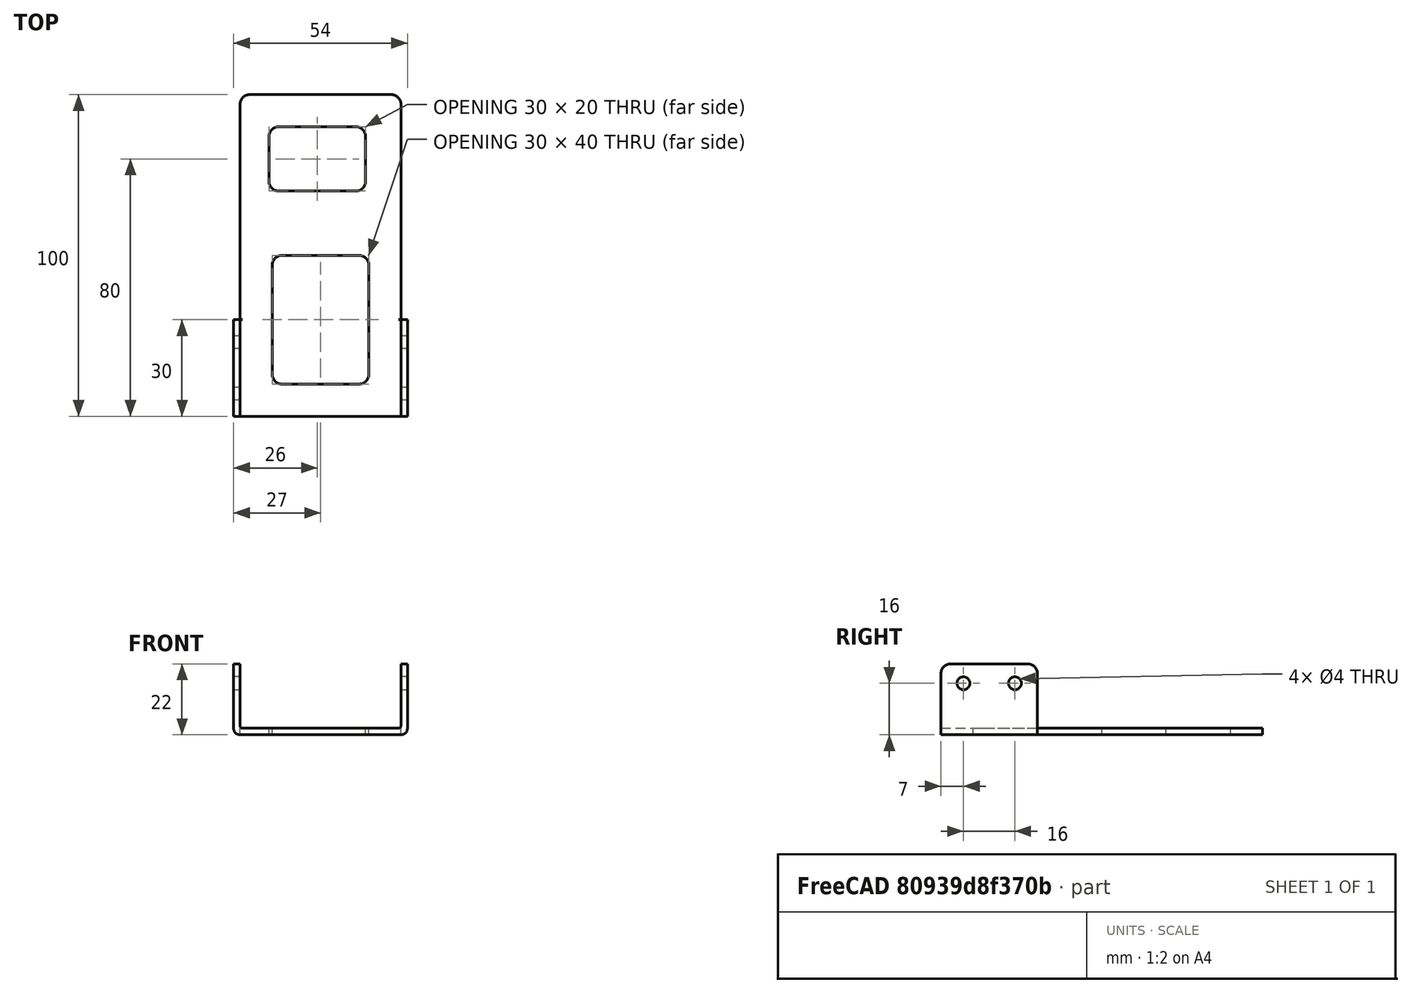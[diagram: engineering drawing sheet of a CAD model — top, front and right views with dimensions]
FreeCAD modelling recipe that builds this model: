
FCSTD DOCUMENT  (FreeCAD 1.0R39285 (Git))
Label: ojt1_t12r03_universal_support
License: All rights reserved
objects: Part::Fillet×7, Part::Box×5, Part::Cut×3, Part::MultiFuse×2, Part::Cylinder×2
note: 19 computed .brp shape members not serialized (recipe doc carries the construction recipe); baked Part::Feature solids carry a one-line shape summary decoded from their .brp

FEATURE [Part::Box] Box  label="basis"
  AttacherType = Attacher::AttachEngine3D
  Height = 2
  Length = 50
  Width = 100
FEATURE [Part::Box] Box001  label="ear_1"
  AttacherType = Attacher::AttachEngine3D
  Height = 22
  Length = 2
  Placement = pos=(50,0,0) rot=(0,0,1;0rad)
  Width = 30
FEATURE [Part::Box] Box002  label="ear_002"
  AttacherType = Attacher::AttachEngine3D
  Height = 22
  Length = 2
  Placement = pos=(-2,0,0) rot=(0,0,1;0rad)
  Width = 30
FEATURE [Part::Fillet] Fillet
  Base = -> Box002
  EdgeLinks = -> Box002 [Edge4]
  Edges = 1 edges r=1.9: [Edge4]
FEATURE [Part::Fillet] Fillet001
  Base = -> Box001
  EdgeLinks = -> Box001 [Edge8]
  Edges = 1 edges r=1.9: [Edge8]
FEATURE [Part::MultiFuse] Fusion
  Refine = true
  Shapes = -> [Box,Fillet,Fillet001]
FEATURE [Part::Fillet] Fillet002
  Base = -> Fusion
  EdgeLinks = -> Fusion [Edge10,Edge12]
  Edges = 2 edges r=0.8: [Edge10,Edge12]
FEATURE [Part::Cylinder] Cylinder  label="Cilindre"
  Angle = 360
  AttacherType = Attacher::AttachEngine3D
  FirstAngle = 0
  Height = 59
  Placement = pos=(-4,7,13) rot=(0,1,0;1.5708rad)
  Radius = 2
  SecondAngle = 0
FEATURE [Part::Cylinder] Cylinder001  label="Cilindre001"
  Angle = 360
  AttacherType = Attacher::AttachEngine3D
  FirstAngle = 0
  Height = 59
  Placement = pos=(-4,23,13) rot=(0,1,0;1.5708rad)
  Radius = 2
  SecondAngle = 0
FEATURE [Part::MultiFuse] Fusion001  label="cylinders"
  Placement = pos=(0,0,3) rot=(0,0,1;0rad)
  Refine = true
  Shapes = -> [Cylinder,Cylinder001]
FEATURE [Part::Cut] Cut
  Base = -> Fillet002
  Refine = true
  Tool = -> Fusion001
FEATURE [Part::Fillet] Fillet003
  Base = -> Cut
  EdgeLinks = -> Cut [Edge3,Edge17,Edge39,Edge47]
  Edges = 4 edges r=3: [Edge3,Edge17,Edge39,Edge47]
FEATURE [Part::Fillet] Fillet004
  Base = -> Fillet003
  EdgeLinks = -> Fillet003 [Edge34,Edge57]
  Edges = 2 edges r=3: [Edge34,Edge57]
FEATURE [Part::Box] Box003  label="Cub"
  AttacherType = Attacher::AttachEngine3D
  Height = 6
  Length = 30
  Placement = pos=(10,10,-2) rot=(0,0,1;0rad)
  Width = 40
FEATURE [Part::Cut] Cut001
  Base = -> Fillet004
  Refine = true
  Tool = -> Box003
FEATURE [Part::Fillet] Fillet005
  Base = -> Cut001
  EdgeLinks = -> Cut001 [Edge51,Edge52,Edge54,Edge56]
  Edges = 4 edges r=3: [Edge51,Edge52,Edge54,Edge56]
FEATURE [Part::Box] Box004  label="Cub001"
  AttacherType = Attacher::AttachEngine3D
  Height = 7
  Length = 30
  Placement = pos=(9,70,-3) rot=(0,0,1;0rad)
  Width = 20
FEATURE [Part::Cut] Cut002
  Base = -> Fillet005
  Refine = true
  Tool = -> Box004
FEATURE [Part::Fillet] Fillet006  label="universal_suport"
  Base = -> Cut002
  EdgeLinks = -> Cut002 [Edge75,Edge76,Edge78,Edge80]
  Edges = 4 edges r=3: [Edge75,Edge76,Edge78,Edge80]
